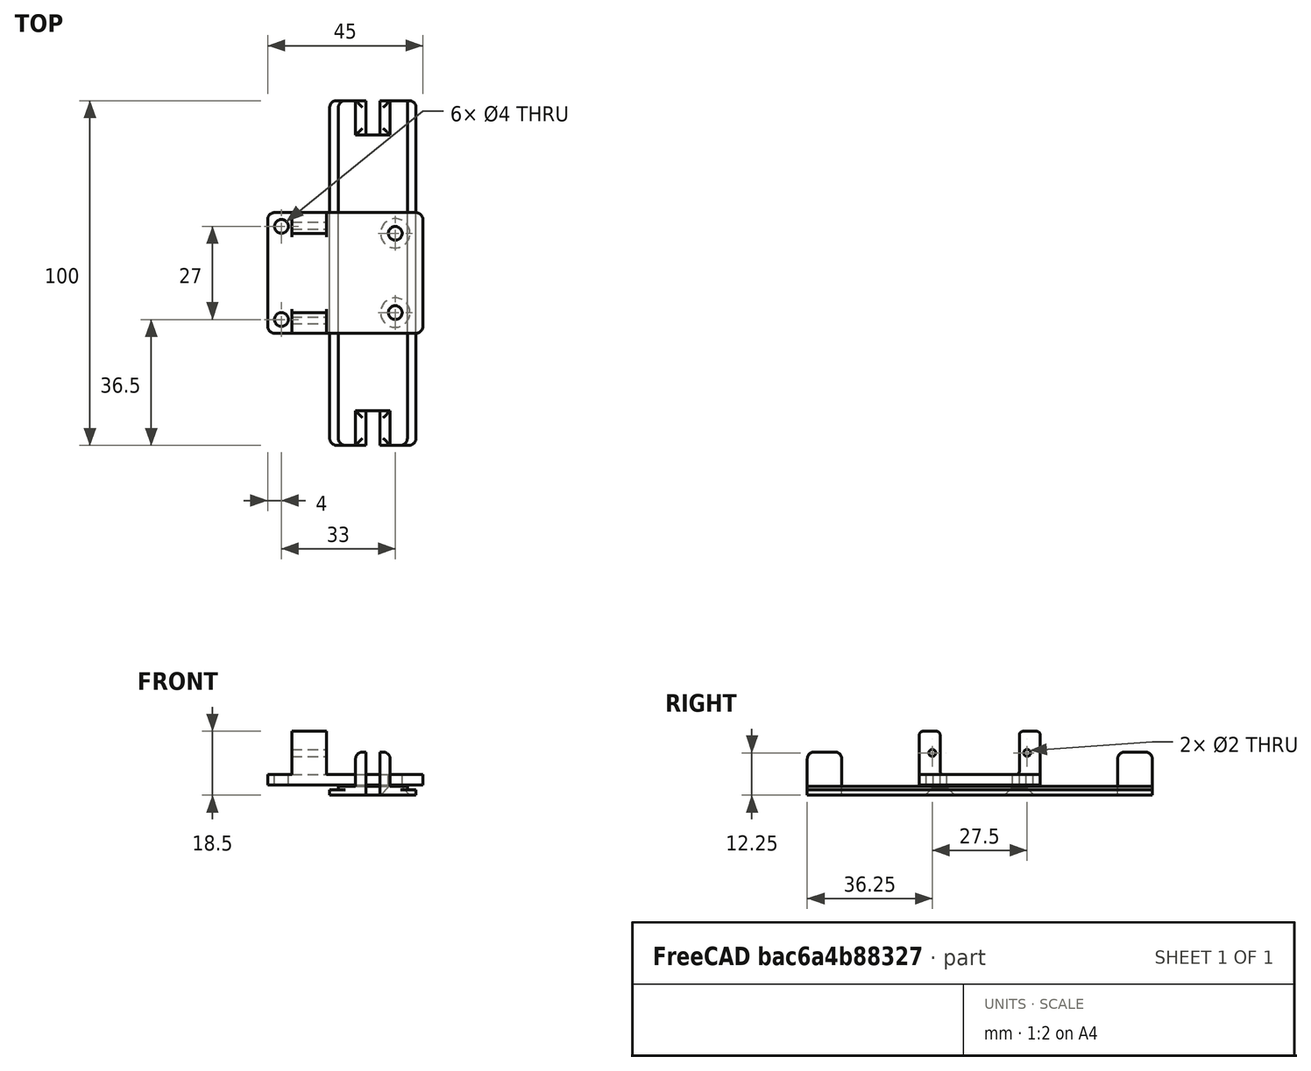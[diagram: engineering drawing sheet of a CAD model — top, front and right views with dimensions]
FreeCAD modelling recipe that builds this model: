
FCSTD DOCUMENT  (FreeCAD 0.19R24276 (Git))
Label: ServoBase
License: All rights reserved
LicenseURL: http://en.wikipedia.org/wiki/All_rights_reserved
objects: Part::Box×9, Part::Cylinder×8, Part::Fillet×6, Part::MultiFuse×6, Part::Cut×4, Spreadsheet::Sheet×1, Part::Chamfer×1
note: 34 computed .brp shape members not serialized (recipe doc carries the construction recipe); baked Part::Feature solids carry a one-line shape summary decoded from their .brp

FEATURE [Part::Box] Box  label="base"
  AttacherType = Attacher::AttachEngine3D
  Height = 3
  Length = 45
  Width = 35
  expr: Width = <<data>>.base_width
  expr: Length = <<data>>.base_depth
FEATURE [Part::Box] Box001  label="Cube"
  AttacherType = Attacher::AttachEngine3D
  Height = 12.5
  Length = 10
  Placement = pos=(7,0,3) rot=(0,0,1;0rad)
  Width = 35
  expr: .Placement.Base.y = (<<data>>.base_width - 35mm) / 2
FEATURE [Part::Box] Box002  label="Cube001"
  AttacherType = Attacher::AttachEngine3D
  Height = 12.5
  Length = 16
  Placement = pos=(7,6,3) rot=(0,0,1;0rad)
  Width = 23
  expr: .Placement.Base.y = (<<data>>.base_width - 35mm) / 2 + 6mm
FEATURE [Part::Cut] Cut
  Base = -> Box001
  Tool = -> Box002
FEATURE [Part::Cylinder] Cylinder
  Angle = 360
  AttacherType = Attacher::AttachEngine3D
  Height = 28
  Placement = pos=(0,3.75,9.25) rot=(0,1,0;1.5708rad)
  Radius = 1
  expr: .Placement.Base.y = <<data>>.base_width / 2 - <<data>>.hole_width / 2
FEATURE [Part::Cylinder] Cylinder001
  Angle = 360
  AttacherType = Attacher::AttachEngine3D
  Height = 28
  Placement = pos=(0,31.25,9.25) rot=(0,1,0;1.5708rad)
  Radius = 1
  expr: .Placement.Base.y = <<data>>.base_width / 2 + <<data>>.hole_width / 2
FEATURE [Part::Cylinder] Cylinder002
  Angle = 360
  AttacherType = Attacher::AttachEngine3D
  Height = 10
  Placement = pos=(4,4,0) rot=(0,0,1;0rad)
  Radius = 2
  expr: .Placement.Base.y = 4mm
FEATURE [Part::Cylinder] Cylinder003
  Angle = 360
  AttacherType = Attacher::AttachEngine3D
  Height = 10
  Placement = pos=(4,31,0) rot=(0,0,1;0rad)
  Radius = 2
  expr: .Placement.Base.y = <<data>>.base_width - 4mm
FEATURE [Part::Cylinder] Cylinder004
  Angle = 360
  AttacherType = Attacher::AttachEngine3D
  Height = 10
  Placement = pos=(37,6,-5) rot=(0,0,1;0rad)
  Radius = 2
  expr: .Placement.Base.x = <<data>>.base_depth - 8mm
FEATURE [Part::Cylinder] Cylinder005
  Angle = 360
  AttacherType = Attacher::AttachEngine3D
  Height = 10
  Placement = pos=(37,29,-5) rot=(0,0,1;0rad)
  Radius = 2
  expr: .Placement.Base.y = <<data>>.base_width - 6mm
  expr: .Placement.Base.x = <<data>>.base_depth - 8mm
FEATURE [Part::Fillet] Fillet
  Base = -> Box
  Edges = 4 edges r=2: [Edge1,Edge3,Edge5,Edge7]
FEATURE [Part::MultiFuse] Fusion001
  Shapes = -> [Cylinder002,Cylinder,Cylinder004,Cylinder005,Cylinder003,Cylinder001]
FEATURE [Spreadsheet::Sheet] Spreadsheet  label="data"
  cells = A2=base_width; B2(base_width)==35mm; A3=hole_width; B3(hole_width)==27.5mm; A4=base_depth; B4(base_depth)==45mm
FEATURE [Part::MultiFuse] Fusion
  Shapes = -> [Fillet,Cut]
FEATURE [Part::Cut] Cut001
  Base = -> Fusion
  Tool = -> Fusion001
FEATURE [Part::Box] Box003  label="Cube002"
  AttacherType = Attacher::AttachEngine3D
  Height = 1.5
  Length = 25
  Placement = pos=(18,-32.5,-3) rot=(0,0,1;0rad)
  Width = 100
  expr: .Placement.Base.y = -(100mm - <<data>>.base_width) / 2
  expr: Width = 100mm
FEATURE [Part::Box] Box004  label="Cube003"
  AttacherType = Attacher::AttachEngine3D
  Height = 1
  Length = 20
  Placement = pos=(20.5,-32.5,-1.5) rot=(0,0,1;0rad)
  Width = 100
  expr: .Placement.Base.y = -(100mm - <<data>>.base_width) / 2
FEATURE [Part::Fillet] Fillet001
  Base = -> Box003
  Edges = 4 edges r=2: [Edge1,Edge3,Edge5,Edge7]
FEATURE [Part::Fillet] Fillet002
  Base = -> Box004
  Edges = 3 edges r=2: [Edge1,Edge3,Edge5]
FEATURE [Part::Cylinder] Cylinder006
  Angle = 360
  AttacherType = Attacher::AttachEngine3D
  Height = 10
  Placement = pos=(37,29,-5) rot=(0,0,1;0rad)
  Radius = 2
  expr: .Placement.Base.x = <<data>>.base_depth - 8mm
  expr: .Placement.Base.y = <<data>>.base_width - 6mm
FEATURE [Part::Cylinder] Cylinder007
  Angle = 360
  AttacherType = Attacher::AttachEngine3D
  Height = 10
  Placement = pos=(37,6,-5) rot=(0,0,1;0rad)
  Radius = 2
  expr: .Placement.Base.x = <<data>>.base_depth - 8mm
FEATURE [Part::MultiFuse] Fusion002
  Shapes = -> [Cylinder006,Cylinder007]
FEATURE [Part::MultiFuse] Fusion003
  Shapes = -> [Fillet002,Fillet001]
FEATURE [Part::Cut] Cut002
  Base = -> Fusion003
  Tool = -> Fusion002
FEATURE [Part::Box] Box005  label="Cube004"
  AttacherType = Attacher::AttachEngine3D
  Height = 10
  Length = 10
  Placement = pos=(25.5,-32.5,-0.5) rot=(0,0,1;0rad)
  Width = 10
  expr: .Placement.Base.y = -(100mm - <<data>>.base_width) / 2
FEATURE [Part::Fillet] Fillet003
  Base = -> Box005
  Edges = 4 edges r=2: [Edge2,Edge6,Edge10,Edge12]
FEATURE [Part::Box] Box006  label="Cube005"
  AttacherType = Attacher::AttachEngine3D
  Height = 10
  Length = 10
  Placement = pos=(25.5,57.5,-0.5) rot=(0,0,1;0rad)
  Width = 10
  expr: .Placement.Base.y = <<data>>.base_width / 2 + 40mm
FEATURE [Part::Fillet] Fillet004
  Base = -> Box006
  Edges = 4 edges r=2: [Edge2,Edge6,Edge10,Edge12]
FEATURE [Part::Box] Box007  label="Cube006"
  AttacherType = Attacher::AttachEngine3D
  Height = 13
  Length = 4
  Placement = pos=(28.5,-32.5,-3) rot=(0,0,1;0rad)
  Width = 10
  expr: .Placement.Base.y = -(100mm - <<data>>.base_width) / 2
FEATURE [Part::Box] Box008  label="Cube007"
  AttacherType = Attacher::AttachEngine3D
  Height = 13
  Length = 4
  Placement = pos=(28.5,57.5,-3) rot=(0,0,1;0rad)
  Width = 10
  expr: .Placement.Base.y = <<data>>.base_width / 2 + 40mm
FEATURE [Part::MultiFuse] Fusion004
  Shapes = -> [Cut002,Fillet003,Fillet004]
FEATURE [Part::MultiFuse] Fusion005
  Shapes = -> [Box008,Box007]
FEATURE [Part::Cut] Cut003
  Base = -> Fusion004
  Tool = -> Fusion005
FEATURE [Part::Chamfer] Chamfer  label="BOTTOM"
  Base = -> Cut003
  Edges = 2 edges r=2.25: [Edge28,Edge29]
FEATURE [Part::Fillet] Fillet005  label="TOP"
  Base = -> Cut001
  Edges = 6 edges r=1: [Edge11,Edge12,Edge50,Edge52,Edge65,Edge66]
